# Revit family: QF_MACOM_FE09E_DA
name_source: partatom
category: Equipamento especial
units: mm (PartAtom-declared; Revit-internal decimal feet)

## family parameters
Com base no plano de trabalho = Não
Compartilhado = Não
Corte com vazios quando carregada = Não
Cota do conector redondo = Utilizar diâmetro
Número OmniClass = 23.40.40.14.17.11
Ponto de cálculo do ambiente = Não
Sempre na vertical = Sim
Tipo de parte = Normal
Título OmniClass = Cookers, Ovens, Stoves

## types (2) — shared parameters
Descrição = FOGAO ENCOSTO EXPORTACAO MACOM 915, DUPLO GAS, PADRAO GLP + KIT GAS NATURAL- MEDINDO: 915X686X328
Elevação padrão = 0,000 mm
Fabricante = MACOM
Gas Connection Height = 80,000 mm
Height = 328,000 mm
Length = 686,000 mm
Modelo = FE09E-DA
Number of Burners = 06
URL = https://www.acosmacom.com.br
Volume = 0,21 m³
Weight = 53,00 kg
Width = 915,000 mm

## per-type parameters (varying)
| type | Gas Consumption GLP | Gas Consumtion GN | Gas Input GLP | Gas Input GN | Gas Pressure | Gas Size |
| FE09E-G | 2,25 Kg/h | 0,00 m³/h | 102508 Btu/h |  | 0,03 bar | 1" |
| FE09E-N |  | 2,71 m³/h | 0 Btu/h | 25934 kcal/h | 0,02 bar | 0" |

## geometry (parser evidence)
native form markers: Sweep x11
no freeform markers — native parametric forms only
